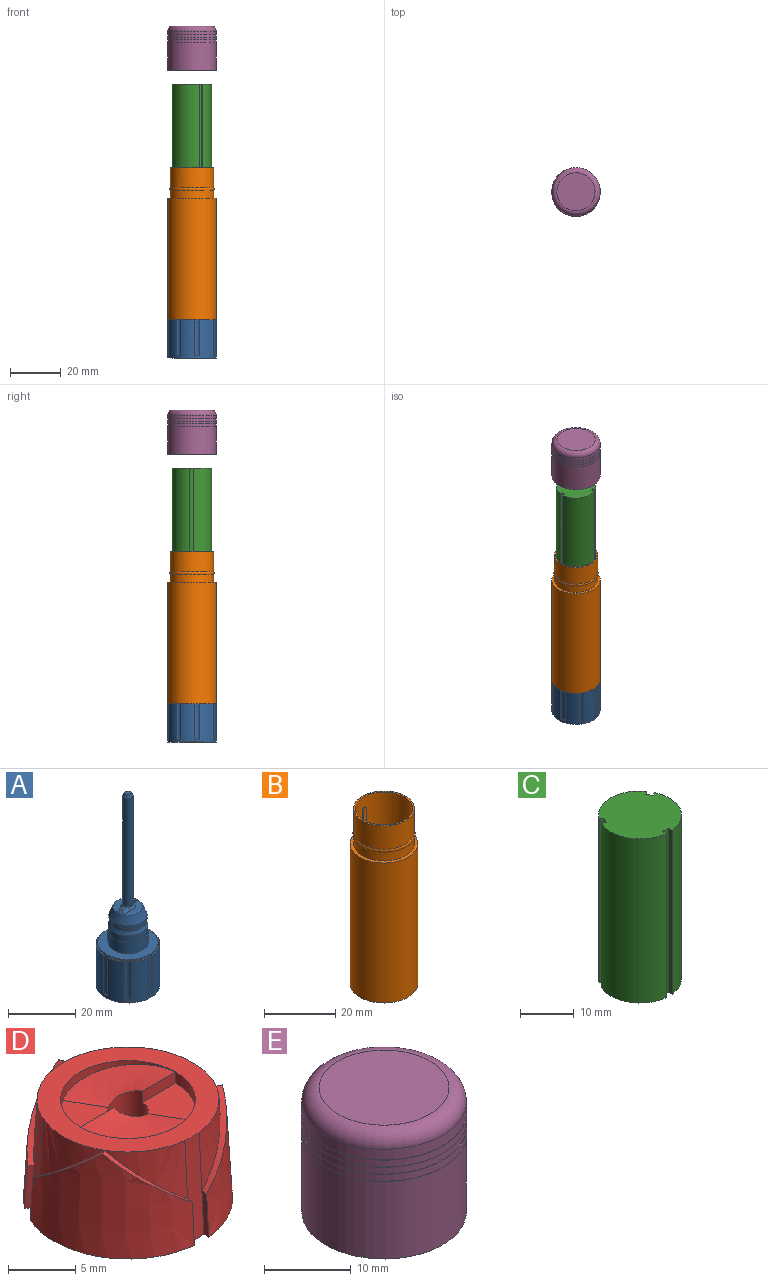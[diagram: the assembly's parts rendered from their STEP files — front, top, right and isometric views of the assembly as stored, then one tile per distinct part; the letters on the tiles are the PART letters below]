
ASSEMBLY  parts=5 mates=4
PART A: 97 faces, bbox 19.1x19.1x70.1 mm
  f0: plane 8.54x4.51mm, normal (0,0,1), area 19mm2, adj f40,f87,f92,f95
  f1: plane 8.54x4.51mm, normal (0,0,1), area 19mm2, adj f40,f88,f91,f96
  f2: cylinder r=1.5mm len=39.5mm, axis (0,0,-1), area 372.3mm2, adj f41,f89,f93,f95,f96
  f3: plane 16.01x16.01mm, normal (0,0,-1), area 114.5mm2, adj f30,f43,f47,f50,f51,f52,f55,f56
  f4: plane 6.36x3.08mm, normal (0,0,1), area 2.9mm2, adj f13,f15,f25,f32
  f5: plane 6.36x3.08mm, normal (0,0,1), area 2.9mm2, adj f15,f17,f25,f32
  f6: plane 6.36x3.08mm, normal (0,0,1), area 2.9mm2, adj f17,f19,f25,f32
  f7: plane 6.36x3.08mm, normal (0,0,1), area 2.9mm2, adj f19,f21,f25,f32
  f8: plane 6.36x3.08mm, normal (0,0,1), area 2.9mm2, adj f21,f23,f25,f32
  f9: plane 6.36x3.08mm, normal (0,0,1), area 2.9mm2, adj f23,f25,f28,f32
  f10: plane 6.36x3.08mm, normal (0,0,1), area 2.9mm2, adj f11,f25,f28,f32
  f11: cylinder r=1.34mm len=14mm, axis (0,0,-1), area 31.6mm2, adj f10,f12,f25,f26
  f12: plane 1.42x1.42mm, normal (0,0,1), area 0.7mm2, adj f11,f25
  f13: cylinder r=1.34mm len=14mm, axis (0,0,-1), area 31.6mm2, adj f4,f14,f25,f26
  f14: plane 2x0.5mm, normal (0,0,1), area 0.7mm2, adj f13,f25
  f15: cylinder r=1.34mm len=14mm, axis (0,0,-1), area 31.6mm2, adj f4,f5,f16,f25
  f16: plane 1.42x1.42mm, normal (0,0,1), area 0.7mm2, adj f15,f25
  f17: cylinder r=1.34mm len=14mm, axis (0,0,-1), area 31.6mm2, adj f5,f6,f18,f25
  f18: plane 2x0.5mm, normal (0,0,1), area 0.7mm2, adj f17,f25
  f19: cylinder r=1.34mm len=14mm, axis (0,0,-1), area 31.6mm2, adj f6,f7,f20,f25
  f20: plane 1.42x1.42mm, normal (0,0,1), area 0.7mm2, adj f19,f25
  f21: cylinder r=1.34mm len=14mm, axis (0,0,-1), area 31.6mm2, adj f7,f8,f22,f25
  f22: plane 2x0.5mm, normal (0,0,1), area 0.7mm2, adj f21,f25
  f23: cylinder r=1.34mm len=14mm, axis (0,0,-1), area 31.6mm2, adj f8,f9,f24,f25
  f24: plane 1.42x1.42mm, normal (0,0,1), area 0.7mm2, adj f23,f25
  f25: cylinder r=9.5mm len=19mm, axis (0,0,-1), area 670.9mm2, adj f4,f5,f6,f7,f8,f9,f10,f11
  f26: plane 6.36x3.08mm, normal (0,0,1), area 2.9mm2, adj f11,f13,f25,f32
  f27: plane 19x19mm, normal (0,0,-1), area 82.5mm2, adj f25,f30
  f28: cylinder r=1.34mm len=14mm, axis (0,0,-1), area 31.6mm2, adj f9,f10,f25,f29
  f29: plane 2x0.5mm, normal (0,0,1), area 0.7mm2, adj f25,f28
  f30: cylinder r=8mm len=16mm, axis (0,0,-1), area 710mm2, adj f3,f27,f49,f50,f51,f54,f55,f56
  f31: plane 18x18mm, normal (0,0,1), area 141.4mm2, adj f32,f33
  f32: cylinder r=9mm len=18mm, axis (0,0,-1), area 28.3mm2, adj f4,f5,f6,f7,f8,f9,f10,f26
  f33: cylinder r=6mm len=12mm, axis (0,0,-1), area 150.8mm2, adj f31,f34
  f34: plane 12x12mm, normal (0,0,1), area 3.7mm2, adj f33,f35
  f35: cylinder r=5.9mm len=11.8mm, axis (0,0,-1), area 92.7mm2, adj f34,f36
  f36: cone r=5.9mm half-angle=21.8deg, axis (0,0,-1), area 47.8mm2, adj f35,f37
  f37: cylinder r=5.4mm len=10.8mm, axis (0,0,-1), area 42.4mm2, adj f36,f39
  f38: cylinder r=5.7mm len=11.4mm, axis (0,0,-1), area 35.8mm2, adj f39,f40
  f39: plane 11.4x11.4mm, normal (0,0,-1), area 10.5mm2, adj f37,f38
  f40: cone r=4.5mm half-angle=21.8deg, axis (0,0,-1), area 103.5mm2, adj f0,f1,f38,f90,f94
  f41: cone r=1mm half-angle=26.6deg, axis (0,0,-1), area 8.8mm2, adj f2,f42
  f42: plane 2x2mm, normal (0,0,1), area 3.1mm2, adj f41
  f43: cylinder r=5mm len=10mm, axis (0,0,1), area 206mm2, adj f3,f44
  f44: cone r=5mm half-angle=21.8deg, axis (0,0,-1), area 47.7mm2, adj f43,f45
  f45: cylinder r=4.4mm len=8.8mm, axis (0,0,1), area 122.8mm2, adj f44,f46
  f46: plane 8.8x8.8mm, normal (0,0,-1), area 60.8mm2, adj f45
  f47: plane 10x0.5mm, normal (0,-1,0), area 5mm2, adj f3,f48,f50,f51
  f48: cylinder r=1mm len=1mm, axis (-1,0,0), area 0.8mm2, adj f47,f49,f50,f51
  f49: plane 1.01x0.51mm, normal (0,0,-1), area 0.5mm2, adj f30,f48,f50,f51
  f50: plane 11.01x2.01mm, normal (1,0,0), area 21.8mm2, adj f3,f30,f47,f48,f49
  f51: plane 11.01x2.01mm, normal (-1,0,0), area 21.8mm2, adj f3,f30,f47,f48,f49
  f52: plane 10x0.35mm, normal (-0.71,-0.71,0), area 5mm2, adj f3,f53,f55,f56
  f53: cylinder r=1mm len=1.06mm, axis (-0.71,0.71,0), area 0.8mm2, adj f52,f54,f55,f56
  f54: plane 1.07x1.07mm, normal (0,0,-1), area 0.5mm2, adj f30,f53,f55,f56
  f55: plane 11.01x1.42mm, normal (0.71,-0.71,0), area 21.8mm2, adj f3,f30,f52,f53,f54
  f56: plane 11.01x1.42mm, normal (-0.71,0.71,0), area 21.8mm2, adj f3,f30,f52,f53,f54
  f57: plane 10x0.5mm, normal (-1,0,0), area 5mm2, adj f3,f58,f60,f61
  f58: cylinder r=1mm len=1mm, axis (0,1,0), area 0.8mm2, adj f57,f59,f60,f61
  f59: plane 1.01x0.51mm, normal (0,0,-1), area 0.5mm2, adj f30,f58,f60,f61
  f60: plane 11.01x2.01mm, normal (0,-1,0), area 21.8mm2, adj f3,f30,f57,f58,f59
  f61: plane 11.01x2.01mm, normal (0,1,0), area 21.8mm2, adj f3,f30,f57,f58,f59
  f62: plane 10x0.35mm, normal (-0.71,0.71,0), area 5mm2, adj f3,f63,f65,f66
  f63: cylinder r=1mm len=1.06mm, axis (0.71,0.71,0), area 0.8mm2, adj f62,f64,f65,f66
  f64: plane 1.07x1.07mm, normal (0,0,-1), area 0.5mm2, adj f30,f63,f65,f66
  f65: plane 11.01x1.42mm, normal (-0.71,-0.71,0), area 21.8mm2, adj f3,f30,f62,f63,f64
  f66: plane 11.01x1.42mm, normal (0.71,0.71,0), area 21.8mm2, adj f3,f30,f62,f63,f64
  f67: plane 10x0.5mm, normal (0,1,0), area 5mm2, adj f3,f68,f70,f71
  f68: cylinder r=1mm len=1mm, axis (1,0,0), area 0.8mm2, adj f67,f69,f70,f71
  f69: plane 1.01x0.51mm, normal (0,0,-1), area 0.5mm2, adj f30,f68,f70,f71
  f70: plane 11.01x2.01mm, normal (-1,0,0), area 21.8mm2, adj f3,f30,f67,f68,f69
  f71: plane 11.01x2.01mm, normal (1,0,0), area 21.8mm2, adj f3,f30,f67,f68,f69
  f72: plane 10x0.35mm, normal (0.71,0.71,0), area 5mm2, adj f3,f73,f75,f76
  f73: cylinder r=1mm len=1.06mm, axis (0.71,-0.71,0), area 0.8mm2, adj f72,f74,f75,f76
  f74: plane 1.07x1.07mm, normal (0,0,-1), area 0.5mm2, adj f30,f73,f75,f76
  f75: plane 11.01x1.42mm, normal (-0.71,0.71,0), area 21.8mm2, adj f3,f30,f72,f73,f74
  f76: plane 11.01x1.42mm, normal (0.71,-0.71,0), area 21.8mm2, adj f3,f30,f72,f73,f74
  f77: plane 10x0.5mm, normal (1,0,0), area 5mm2, adj f3,f78,f80,f81
  f78: cylinder r=1mm len=1mm, axis (0,-1,0), area 0.8mm2, adj f77,f79,f80,f81
  f79: plane 1.01x0.51mm, normal (0,0,-1), area 0.5mm2, adj f30,f78,f80,f81
  f80: plane 11.01x2.01mm, normal (0,1,0), area 21.8mm2, adj f3,f30,f77,f78,f79
  f81: plane 11.01x2.01mm, normal (0,-1,0), area 21.8mm2, adj f3,f30,f77,f78,f79
  f82: plane 10x0.35mm, normal (0.71,-0.71,0), area 5mm2, adj f3,f83,f85,f86
  f83: cylinder r=1mm len=1.06mm, axis (-0.71,-0.71,0), area 0.8mm2, adj f82,f84,f85,f86
  f84: plane 1.07x1.07mm, normal (0,0,-1), area 0.5mm2, adj f30,f83,f85,f86
  f85: plane 11.01x1.42mm, normal (0.71,0.71,0), area 21.8mm2, adj f3,f30,f82,f83,f84
  f86: plane 11.01x1.42mm, normal (-0.71,-0.71,0), area 21.8mm2, adj f3,f30,f82,f83,f84
  f87: plane 3x1mm, normal (0,1,0), area 2.1mm2, adj f0,f89,f90,f95
  f88: plane 3.07x1.07mm, normal (0,-0.71,0.71), area 3.7mm2, adj f1,f89,f90,f96
  f89: plane 2.38x1mm, normal (0,0,1), area 2.1mm2, adj f2,f87,f88,f90
  f90: bspline ~2x1.15mm, area 2.2mm2, adj f40,f87,f88,f89
  f91: plane 3x1mm, normal (0,-1,0), area 2.1mm2, adj f1,f93,f94,f96
  f92: plane 3.08x1.07mm, normal (0,0.71,0.71), area 3.7mm2, adj f0,f93,f94,f95
  f93: plane 2.38x1mm, normal (0,0,1), area 2.1mm2, adj f2,f91,f92,f94
  f94: bspline ~2x1.15mm, area 2.2mm2, adj f40,f91,f92,f93
  f95: cone r=1.5mm half-angle=36.9deg, axis (0,0,-1), area 5.2mm2, adj f0,f2,f87,f92
  f96: cone r=1.5mm half-angle=36.9deg, axis (0,0,-1), area 5.2mm2, adj f1,f2,f88,f91
PART B: 32 faces, bbox 19x19x60 mm
  f0: cylinder r=8.5mm len=17mm, axis (0,0,1), area 427.3mm2, adj f17,f31
  f1: cylinder r=0.5mm len=0.71mm, axis (0.83,0.55,0), area 0.4mm2, adj f2,f3,f5,f13
  f2: cylinder r=0.5mm len=0.68mm, axis (-0.9,-0.44,0), area 0.4mm2, adj f1,f3,f4,f13
  f3: cylinder r=7.5mm len=47.5mm, axis (0,0,1), area 44.5mm2, adj f1,f2,f4,f5,f11
  f4: plane 47x0.45mm, normal (-0.44,0.9,0), area 23.5mm2, adj f2,f3,f11,f13
  f5: plane 47x0.42mm, normal (0.55,-0.83,0), area 23.5mm2, adj f1,f3,f11,f13
  f6: cylinder r=0.5mm len=0.68mm, axis (-0.9,0.44,0), area 0.4mm2, adj f7,f8,f10,f13
  f7: cylinder r=0.5mm len=0.71mm, axis (0.83,-0.55,0), area 0.4mm2, adj f6,f8,f9,f13
  f8: cylinder r=7.5mm len=47.5mm, axis (0,0,1), area 44.5mm2, adj f6,f7,f9,f10,f11
  f9: plane 47x0.42mm, normal (-0.55,-0.83,0), area 23.5mm2, adj f7,f8,f11,f13
  f10: plane 47x0.45mm, normal (0.44,0.9,0), area 23.5mm2, adj f6,f8,f11,f13
  f11: plane 16x15.98mm, normal (0,0,1), area 104.6mm2, adj f3,f4,f5,f8,f9,f10,f13,f22
  f12: cylinder r=8mm len=16mm, axis (0,0,1), area 351.9mm2, adj f19,f21
  f13: cylinder r=8mm len=51mm, axis (0,0,1), area 2421.3mm2, adj f1,f2,f4,f5,f6,f7,f9,f10
  f14: cylinder r=9.5mm len=48mm, axis (0,0,1), area 2865.1mm2, adj f15,f18
  f15: plane 19x19mm, normal (0,0,1), area 56.5mm2, adj f14,f16
  f16: cylinder r=8.5mm len=17mm, axis (0,0,1), area 160.2mm2, adj f15,f31
  f17: plane 17x17mm, normal (0,0,1), area 25.9mm2, adj f0,f13
  f18: plane 19x19mm, normal (0,0,-1), area 29.1mm2, adj f14,f20
  f19: plane 18x18mm, normal (0,0,-1), area 53.4mm2, adj f12,f20
  f20: cylinder r=9mm len=18mm, axis (0,0,-1), area 56.5mm2, adj f18,f19
  f21: plane 16x16mm, normal (0,0,-1), area 68.3mm2, adj f12,f29
  f22: plane 47x0.5mm, normal (-1,-0.06,0), area 23.5mm2, adj f11,f13,f24,f25
  f23: plane 47x0.5mm, normal (1,-0.06,0), area 23.5mm2, adj f11,f13,f24,f26
  f24: cylinder r=7.5mm len=47.5mm, axis (0,0,1), area 44.5mm2, adj f11,f22,f23,f25,f26
  f25: cylinder r=0.5mm len=0.55mm, axis (0.06,-1,0), area 0.4mm2, adj f13,f22,f24,f26
  f26: cylinder r=0.5mm len=0.55mm, axis (0.06,1,0), area 0.4mm2, adj f13,f23,f24,f25
  f27: cone r=6mm half-angle=26.6deg, axis (0,0,-1), area 40.4mm2, adj f11,f28
  f28: cylinder r=6mm len=12mm, axis (0,0,1), area 113.1mm2, adj f27,f30
  f29: cylinder r=6.5mm len=13mm, axis (0,0,1), area 122.5mm2, adj f21,f30
  f30: plane 13x13mm, normal (0,0,-1), area 19.6mm2, adj f28,f29
  f31: torus R=7.97mm, axis (0,0,1), area 59.8mm2, adj f0,f16
PART C: 16 faces, bbox 15.5x15.5x37.5 mm
  f0: cylinder r=7.75mm len=37.5mm, axis (0,0,1), area 552.3mm2, adj f4,f9,f12,f13
  f1: cylinder r=7.75mm len=37.5mm, axis (0,0,1), area 552.3mm2, adj f5,f7,f9,f13
  f2: cylinder r=7.75mm len=37.5mm, axis (0,0,1), area 552.3mm2, adj f8,f9,f11,f13
  f3: plane 37.5x1.3mm, normal (0.87,0.5,0), area 56.2mm2, adj f4,f5,f9,f13
  f4: plane 37.5x0.83mm, normal (-0.5,0.87,0), area 36.1mm2, adj f0,f3,f9,f13
  f5: plane 37.5x0.83mm, normal (0.5,-0.87,0), area 36.1mm2, adj f1,f3,f9,f13
  f6: plane 37.5x1.3mm, normal (-0.87,0.5,0), area 56.2mm2, adj f7,f8,f9,f13
  f7: plane 37.5x0.83mm, normal (-0.5,-0.87,0), area 36.1mm2, adj f1,f6,f9,f13
  f8: plane 37.5x0.83mm, normal (0.5,0.87,0), area 36.1mm2, adj f2,f6,f9,f13
  f9: plane 15.5x15.46mm, normal (0,0,1), area 184.2mm2, adj f0,f1,f2,f3,f4,f5,f6,f7
  f10: plane 37.5x1.5mm, normal (0,-1,0), area 56.2mm2, adj f9,f11,f12,f13
  f11: plane 37.5x0.96mm, normal (1,0,0), area 36.1mm2, adj f2,f9,f10,f13
  f12: plane 37.5x0.96mm, normal (-1,0,0), area 36.1mm2, adj f0,f9,f10,f13
  f13: plane 15.5x15.46mm, normal (0,0,-1), area 177.2mm2, adj f0,f1,f2,f3,f4,f5,f6,f7
  f14: plane 3x3mm, normal (0,0,-1), area 7.1mm2, adj f15
  f15: cylinder r=1.5mm len=32.5mm, axis (0,0,1), area 306.3mm2, adj f13,f14
PART D: 122 faces, bbox 16.4x16.3x9 mm
  f0: cylinder r=2.5mm len=5mm, axis (0,0,1), area 30.9mm2, adj f115,f121
  f1: plane 13.52x13.41mm, normal (0,0,-1), area 120.5mm2, adj f4,f6,f9,f21,f23,f26,f38,f40
  f2: plane 2.19x1.29mm, normal (-0.86,-0.5,-0.06), area 1.9mm2, adj f5,f106,f112,f114
  f3: plane 2.19x1.29mm, normal (-0.86,-0.5,-0.06), area 1.9mm2, adj f4,f6,f111,f113
  f4: plane 4.36x0.8mm, normal (0.5,-0.87,0), area 1.9mm2, adj f1,f3,f9,f10,f11,f16,f17,f18
  f5: plane 2.31x0.84mm, normal (-0.5,0.87,0), area 1.1mm2, adj f2,f24,f25,f30,f31,f32,f50,f107
  f6: plane 4.36x0.8mm, normal (-0.5,0.87,0), area 1.9mm2, adj f1,f3,f26,f27,f28,f33,f34,f35
  f7: cone r=6.36mm half-angle=3.2deg, axis (0,0,-1), area 1.2mm2, adj f8,f14,f39,f106
  f8: torus R=7.22mm, axis (0,0,1), area 9.1mm2, adj f7,f39,f50,f106
  f9: cone r=6.87mm half-angle=3.2deg, axis (0,0,-1), area 23.7mm2, adj f1,f4,f18,f40
  f10: cone r=6.36mm half-angle=3.2deg, axis (0,0,-1), area 2.2mm2, adj f4,f17,f18,f40
  f11: cone r=6.98mm half-angle=3.2deg, axis (0,0,-1), area 12.1mm2, adj f4,f16,f17,f40
  f12: cone r=6.36mm half-angle=3.2deg, axis (0,0,-1), area 2.3mm2, adj f15,f16,f90,f109
  f13: cone r=7.1mm half-angle=3.2deg, axis (0,0,-1), area 12.3mm2, adj f14,f15,f39,f106
  f14: torus R=7.12mm, axis (0,0,1), area 7.4mm2, adj f7,f13,f39,f106
  f15: torus R=7.02mm, axis (0,0,1), area 7.3mm2, adj f12,f13,f39,f90,f106,f109
  f16: torus R=7.01mm, axis (0,0,1), area 7.3mm2, adj f4,f11,f12,f40,f90,f109
  f17: torus R=6.91mm, axis (0,0,1), area 7.2mm2, adj f4,f10,f11,f40
  f18: torus R=6.9mm, axis (0,0,1), area 7.1mm2, adj f4,f9,f10,f40
  f19: plane 2.19x1.29mm, normal (0.86,-0.5,-0.06), area 1.9mm2, adj f22,f97,f103,f105
  f20: plane 2.19x1.29mm, normal (0.86,-0.5,-0.06), area 1.9mm2, adj f21,f23,f102,f104
  f21: plane 4.36x0.8mm, normal (0.5,0.87,0), area 1.9mm2, adj f1,f20,f26,f27,f28,f33,f34,f35
  f22: plane 2.31x0.84mm, normal (-0.5,-0.87,0), area 1.1mm2, adj f19,f41,f50,f77,f82,f83,f84,f98
  f23: plane 4.36x0.8mm, normal (-0.5,-0.87,0), area 1.9mm2, adj f1,f20,f78,f79,f80,f85,f86,f87
  f24: cone r=6.36mm half-angle=3.2deg, axis (0,0,-1), area 1.2mm2, adj f5,f25,f31,f97
  f25: torus R=7.22mm, axis (0,0,1), area 9.1mm2, adj f5,f24,f50,f97
  f26: cone r=6.87mm half-angle=3.2deg, axis (0,0,-1), area 23.7mm2, adj f1,f6,f21,f35
  f27: cone r=6.36mm half-angle=3.2deg, axis (0,0,-1), area 2.2mm2, adj f6,f21,f34,f35
  f28: cone r=6.98mm half-angle=3.2deg, axis (0,0,-1), area 12.1mm2, adj f6,f21,f33,f34
  f29: cone r=6.36mm half-angle=3.2deg, axis (0,0,-1), area 2.3mm2, adj f32,f33,f100,f108
  f30: cone r=7.1mm half-angle=3.2deg, axis (0,0,-1), area 12.3mm2, adj f5,f31,f32,f97
  f31: torus R=7.12mm, axis (0,0,1), area 7.4mm2, adj f5,f24,f30,f97
  f32: torus R=7.02mm, axis (0,0,1), area 7.3mm2, adj f5,f29,f30,f97,f100,f108
  f33: torus R=7.01mm, axis (0,0,1), area 7.3mm2, adj f6,f21,f28,f29,f100,f108
  f34: torus R=6.91mm, axis (0,0,1), area 7.2mm2, adj f6,f21,f27,f28
  f35: torus R=6.9mm, axis (0,0,1), area 7.1mm2, adj f6,f21,f26,f27
  f36: plane 2.5x0.77mm, normal (0,1,-0.06), area 1.9mm2, adj f39,f88,f94,f96
  f37: plane 2.5x0.78mm, normal (0,1,-0.06), area 1.9mm2, adj f38,f40,f93,f95
  f38: plane 4.36x0.91mm, normal (-1,0,0), area 1.9mm2, adj f1,f37,f78,f79,f80,f85,f86,f87
  f39: plane 2.31x0.97mm, normal (1,0,0), area 1.1mm2, adj f7,f8,f13,f14,f15,f36,f50,f89
  f40: plane 4.36x0.91mm, normal (1,0,0), area 1.9mm2, adj f1,f9,f10,f11,f16,f17,f18,f37
  f41: cone r=6.36mm half-angle=3.2deg, axis (0,0,-1), area 1.2mm2, adj f22,f77,f83,f88
  f42: cylinder r=5mm len=10mm, axis (0,0,-1), area 10.5mm2, adj f43,f51,f72,f73
  f43: bspline ~7.5x5.77mm, area 24.1mm2, adj f42,f73,f74,f76
  f44: cone r=7.75mm half-angle=3.2deg, axis (0,0,-1), area 91.9mm2, adj f45,f50,f53,f63,f69
  f45: plane 3.84x0.62mm, normal (-0.5,0.87,0), area 1.9mm2, adj f44,f50,f56,f69
  f46: cone r=7.75mm half-angle=3.2deg, axis (0,0,-1), area 91.9mm2, adj f49,f50,f57,f59,f67
  f47: cone r=7.75mm half-angle=3.2deg, axis (0,0,-1), area 91.9mm2, adj f48,f50,f55,f61,f65
  f48: plane 3.84x0.72mm, normal (1,0,0), area 1.9mm2, adj f47,f50,f52,f61
  f49: plane 3.84x0.62mm, normal (-0.5,-0.87,0), area 1.9mm2, adj f46,f50,f54,f59
  f50: plane 15.5x15.47mm, normal (0,0,-1), area 26mm2, adj f5,f8,f22,f25,f39,f44,f45,f46
  f51: plane 13.51x13.5mm, normal (0,0,1), area 64.6mm2, adj f42,f52,f54,f56,f58,f60,f62,f64
  f52: bspline ~9x1.5mm, area 13.5mm2, adj f48,f50,f51,f53,f60,f62
  f53: plane 3.84x0.72mm, normal (-1,0,0), area 1.9mm2, adj f44,f50,f52,f63
  f54: bspline ~9x1.55mm, area 13.5mm2, adj f49,f50,f51,f55,f58,f64
  f55: plane 3.84x0.62mm, normal (0.5,0.87,0), area 1.9mm2, adj f47,f50,f54,f65
  f56: bspline ~9x1.55mm, area 13.5mm2, adj f45,f50,f51,f57,f66,f68
  f57: plane 3.84x0.62mm, normal (0.5,-0.87,0), area 1.9mm2, adj f46,f50,f56,f67
  f58: bspline ~5.68x5.17mm, area 16.6mm2, adj f51,f54,f59
  f59: bspline ~7.57x6.56mm, area 4.1mm2, adj f46,f49,f58,f67
  f60: bspline ~5.34x5.17mm, area 16.6mm2, adj f51,f52,f61
  f61: bspline ~7.57x6.56mm, area 4.1mm2, adj f47,f48,f60,f65
  f62: bspline ~5.34x5.17mm, area 16.6mm2, adj f51,f52,f63
  f63: bspline ~7.57x6.56mm, area 4.1mm2, adj f44,f53,f62,f69
  f64: bspline ~9x8.41mm, area 16.6mm2, adj f51,f54,f65
  f65: bspline ~6.87x5.2mm, area 4.1mm2, adj f47,f55,f61,f64
  f66: bspline ~5.68x5.17mm, area 16.6mm2, adj f51,f56,f67
  f67: bspline ~7.57x6.56mm, area 4.1mm2, adj f46,f57,f59,f66
  f68: bspline ~9x8.41mm, area 16.6mm2, adj f51,f56,f69
  f69: bspline ~6.87x5.2mm, area 4.1mm2, adj f44,f45,f63,f68
  f70: bspline ~7.5x5.77mm, area 24.1mm2, adj f71,f72,f75,f76
  f71: cylinder r=5mm len=10mm, axis (0,0,-1), area 10.5mm2, adj f51,f70,f74,f75
  f72: plane 3.5x1mm, normal (0,-1,0), area 3.5mm2, adj f42,f70,f73,f76
  f73: plane 4.33x4.25mm, normal (0,0,1), area 11.9mm2, adj f42,f43,f72,f76
  f74: plane 3.5x1mm, normal (0,1,0), area 3.5mm2, adj f43,f71,f75,f76
  f75: plane 4.33x4.25mm, normal (0,0,1), area 11.9mm2, adj f70,f71,f74,f76
  f76: cylinder r=1.5mm len=9mm, axis (0,0,1), area 78.5mm2, adj f43,f70,f72,f73,f74,f75,f115
  f77: torus R=7.22mm, axis (0,0,1), area 9.1mm2, adj f22,f41,f50,f88
  f78: cone r=6.87mm half-angle=3.2deg, axis (0,0,-1), area 23.7mm2, adj f1,f23,f38,f87
  f79: cone r=6.36mm half-angle=3.2deg, axis (0,0,-1), area 2.2mm2, adj f23,f38,f86,f87
  f80: cone r=6.98mm half-angle=3.2deg, axis (0,0,-1), area 12.1mm2, adj f23,f38,f85,f86
  f81: cone r=6.36mm half-angle=3.2deg, axis (0,0,-1), area 2.3mm2, adj f84,f85,f91,f99
  f82: cone r=7.1mm half-angle=3.2deg, axis (0,0,-1), area 12.3mm2, adj f22,f83,f84,f88
  f83: torus R=7.12mm, axis (0,0,1), area 7.4mm2, adj f22,f41,f82,f88
  f84: torus R=7.02mm, axis (0,0,1), area 7.3mm2, adj f22,f81,f82,f88,f91,f99
  f85: torus R=7.01mm, axis (0,0,1), area 7.3mm2, adj f23,f38,f80,f81,f91,f99
  f86: torus R=6.91mm, axis (0,0,1), area 7.2mm2, adj f23,f38,f79,f80
  f87: torus R=6.9mm, axis (0,0,1), area 7.1mm2, adj f23,f38,f78,f79
  f88: plane 2.31x0.97mm, normal (-1,0,0), area 1.1mm2, adj f36,f41,f50,f77,f82,f83,f84,f89
  f89: plane 2.5x1.75mm, normal (0,1,-0.06), area 4.4mm2, adj f38,f39,f40,f88,f90,f91,f94,f95
  f90: plane 0.39x0.03mm, normal (-1,0,0), area 0mm2, adj f12,f15,f16,f89
  f91: plane 0.39x0.03mm, normal (1,0,0), area 0mm2, adj f81,f84,f85,f89
  f92: plane 2.5x1.75mm, normal (0,1,-0.06), area 4.4mm2, adj f1,f38,f40,f93
  f93: cylinder r=0.5mm len=2.5mm, axis (1,0,0), area 1.7mm2, adj f37,f38,f40,f92
  f94: cylinder r=0.5mm len=2.5mm, axis (1,0,0), area 1.7mm2, adj f36,f39,f88,f89
  f95: cylinder r=0.5mm len=2.5mm, axis (-1,0,0), area 1.7mm2, adj f37,f38,f40,f89
  f96: cylinder r=0.5mm len=2.5mm, axis (1,0,0), area 1.9mm2, adj f36,f39,f50,f88
  f97: plane 2.31x0.84mm, normal (0.5,0.87,0), area 1.1mm2, adj f19,f24,f25,f30,f31,f32,f50,f98
  f98: plane 2.21x1.75mm, normal (0.86,-0.5,-0.06), area 4.4mm2, adj f21,f22,f23,f97,f99,f100,f103,f104
  f99: plane 0.39x0.03mm, normal (0.5,0.87,0), area 0mm2, adj f81,f84,f85,f98
  f100: plane 0.39x0.03mm, normal (-0.5,-0.87,0), area 0mm2, adj f29,f32,f33,f98
  f101: plane 2.21x1.75mm, normal (0.86,-0.5,-0.06), area 4.4mm2, adj f1,f21,f23,f102
  f102: cylinder r=0.5mm len=2.35mm, axis (-0.5,-0.87,0), area 1.7mm2, adj f20,f21,f23,f101
  f103: cylinder r=0.5mm len=2.35mm, axis (-0.5,-0.87,0), area 1.7mm2, adj f19,f22,f97,f98
  f104: cylinder r=0.5mm len=2.37mm, axis (0.5,0.87,0), area 1.7mm2, adj f20,f21,f23,f98
  f105: cylinder r=0.5mm len=2.41mm, axis (-0.5,-0.87,0), area 1.9mm2, adj f19,f22,f50,f97
  f106: plane 2.31x0.84mm, normal (0.5,-0.87,0), area 1.1mm2, adj f2,f7,f8,f13,f14,f15,f50,f107
  f107: plane 2.21x1.75mm, normal (-0.86,-0.5,-0.06), area 4.4mm2, adj f4,f5,f6,f106,f108,f109,f112,f113
  f108: plane 0.39x0.03mm, normal (0.5,-0.87,0), area 0mm2, adj f29,f32,f33,f107
  f109: plane 0.39x0.03mm, normal (-0.5,0.87,0), area 0mm2, adj f12,f15,f16,f107
  f110: plane 2.21x1.75mm, normal (-0.86,-0.5,-0.06), area 4.4mm2, adj f1,f4,f6,f111
  f111: cylinder r=0.5mm len=2.35mm, axis (-0.5,0.87,0), area 1.7mm2, adj f3,f4,f6,f110
  f112: cylinder r=0.5mm len=2.35mm, axis (-0.5,0.87,0), area 1.7mm2, adj f2,f5,f106,f107
  f113: cylinder r=0.5mm len=2.37mm, axis (0.5,-0.87,0), area 1.7mm2, adj f3,f4,f6,f107
  f114: cylinder r=0.5mm len=2.41mm, axis (-0.5,0.87,0), area 1.9mm2, adj f2,f5,f50,f106
  f115: plane 5x5mm, normal (0,0,-1), area 12.6mm2, adj f0,f76
  f116: cylinder r=2.5mm len=5mm, axis (0,0,1), area 30.9mm2, adj f1,f120
  f117: cylinder r=2mm len=4mm, axis (0,0,-1), area 16.8mm2, adj f118,f119
  f118: torus R=2.5mm, axis (0,0,1), area 6.9mm2, adj f117,f121
  f119: torus R=2.5mm, axis (0,0,1), area 6.9mm2, adj f117,f120
  f120: torus R=2mm, axis (0,0,1), area 7.9mm2, adj f116,f119
  f121: torus R=2mm, axis (0,0,1), area 7.9mm2, adj f0,f118
PART E: 42 faces, bbox 20.6x20.6x17.5 mm
  f0: plane 7.34x0.92mm, normal (0,0,-1), area 0.7mm2, adj f3,f5,f40,f41
  f1: plane 6.36x3.74mm, normal (0,0,-1), area 0.7mm2, adj f2,f16,f36,f41
  f2: torus R=8.6mm, axis (0,0,1), area 1.3mm2, adj f1,f30,f36,f41
  f3: cylinder r=8.7mm len=6.91mm, axis (0,0,1), area 21.3mm2, adj f0,f27,f40,f41
  f4: plane 6.36x3.74mm, normal (0,0,-1), area 0.7mm2, adj f6,f8,f39,f40
  f5: torus R=8.6mm, axis (0,0,1), area 1.3mm2, adj f0,f30,f40,f41
  f6: cylinder r=8.7mm len=5.98mm, axis (0,0,1), area 21.3mm2, adj f4,f27,f39,f40
  f7: plane 6.36x3.74mm, normal (0,0,-1), area 0.7mm2, adj f9,f11,f38,f39
  f8: torus R=8.6mm, axis (0,0,1), area 1.3mm2, adj f4,f30,f39,f40
  f9: cylinder r=8.7mm len=5.98mm, axis (0,0,1), area 21.3mm2, adj f7,f27,f38,f39
  f10: plane 7.34x0.92mm, normal (0,0,-1), area 0.7mm2, adj f12,f15,f37,f38
  f11: torus R=8.6mm, axis (0,0,1), area 1.3mm2, adj f7,f30,f38,f39
  f12: cylinder r=8.7mm len=6.91mm, axis (0,0,1), area 21.3mm2, adj f10,f27,f37,f38
  f13: cylinder r=8.7mm len=5.98mm, axis (0,0,1), area 21.3mm2, adj f14,f27,f36,f37
  f14: plane 6.36x3.74mm, normal (0,0,-1), area 0.7mm2, adj f13,f35,f36,f37
  f15: torus R=8.6mm, axis (0,0,1), area 1.3mm2, adj f10,f30,f37,f38
  f16: cylinder r=8.7mm len=5.98mm, axis (0,0,1), area 21.3mm2, adj f1,f27,f36,f41
  f17: cylinder r=9.5mm len=19mm, axis (0,0,1), area 59.7mm2, adj f19,f24
  f18: plane 19.1x19.1mm, normal (0,0,1), area 3mm2, adj f20,f23
  f19: plane 19.1x19.1mm, normal (0,0,-1), area 3mm2, adj f17,f20
  f20: cylinder r=9.55mm len=19.1mm, axis (0,0,1), area 60mm2, adj f18,f19
  f21: plane 15x15mm, normal (0,0,1), area 176.7mm2, adj f22
  f22: torus R=7.5mm, axis (0,0,1), area 173.2mm2, adj f21,f23
  f23: cylinder r=9.5mm len=19mm, axis (0,0,1), area 89.5mm2, adj f18,f22
  f24: plane 19.1x19.1mm, normal (0,0,1), area 3mm2, adj f17,f26
  f25: plane 19.1x19.1mm, normal (0,0,-1), area 3mm2, adj f26,f28
  f26: cylinder r=9.55mm len=19.1mm, axis (0,0,1), area 60mm2, adj f24,f25
  f27: plane 19x19mm, normal (0,0,-1), area 47.3mm2, adj f3,f6,f9,f12,f13,f16,f28,f36
  f28: cylinder r=9.5mm len=19mm, axis (0,0,1), area 656.6mm2, adj f25,f27
  f29: plane 17.4x17.4mm, normal (0,0,1), area 5.4mm2, adj f33,f34
  f30: cylinder r=8.5mm len=17mm, axis (0,0,1), area 16mm2, adj f2,f5,f8,f11,f15,f34,f35
  f31: plane 15x15mm, normal (0,0,-1), area 176.7mm2, adj f32
  f32: torus R=7.5mm, axis (0,0,1), area 97.9mm2, adj f31,f33
  f33: cylinder r=8.7mm len=17.4mm, axis (0,0,1), area 656mm2, adj f29,f32
  f34: torus R=8.6mm, axis (0,0,1), area 8.4mm2, adj f29,f30
  f35: torus R=8.6mm, axis (0,0,1), area 1.3mm2, adj f14,f30,f36,f37
  f36: cylinder r=3.58mm len=3.1mm, axis (0,0,-1), area 6.2mm2, adj f1,f2,f13,f14,f16,f27,f35
  f37: cylinder r=3.58mm len=3.1mm, axis (0,0,-1), area 6.2mm2, adj f10,f12,f13,f14,f15,f27,f35
  f38: cylinder r=3.58mm len=3.1mm, axis (0,0,-1), area 6.2mm2, adj f7,f9,f10,f11,f12,f15,f27
  f39: cylinder r=3.58mm len=3.1mm, axis (0,0,-1), area 6.2mm2, adj f4,f6,f7,f8,f9,f11,f27
  f40: cylinder r=3.58mm len=3.1mm, axis (0,0,-1), area 6.2mm2, adj f0,f3,f4,f5,f6,f8,f27
  f41: cylinder r=3.58mm len=3.1mm, axis (0,0,-1), area 6.2mm2, adj f0,f1,f2,f3,f5,f16,f27
PLACE A rot(axis=(0,0,1),101.9deg) t=(0,0,-15)mm
PLACE B rot(axis=(0,0,1),87.9deg) t=(0,0,0)mm
PLACE C rot(axis=(0,0,-1),92.5deg) t=(0,0,55.4)mm
PLACE D rot(axis=(0.72,0.69,0),180deg) t=(0,0,55.4)mm
PLACE E rot(axis=(0,0,1),113.7deg) t=(0,0,98.28)mm
MATE cylindrical D.f7 <-> A.f2  axis (0,0,-1) through (0,0,50.87)mm
MATE fastened D.f7 <-> C.f0  axis (0,0,1) through (0,0,55.4)mm
MATE cylindrical B.f0 <-> E.f2  axis (0,0,1) through (0,0,48)mm
MATE revolute B.f20 <-> A.f32  axis (0,0,-1) through (0,0,0)mm
